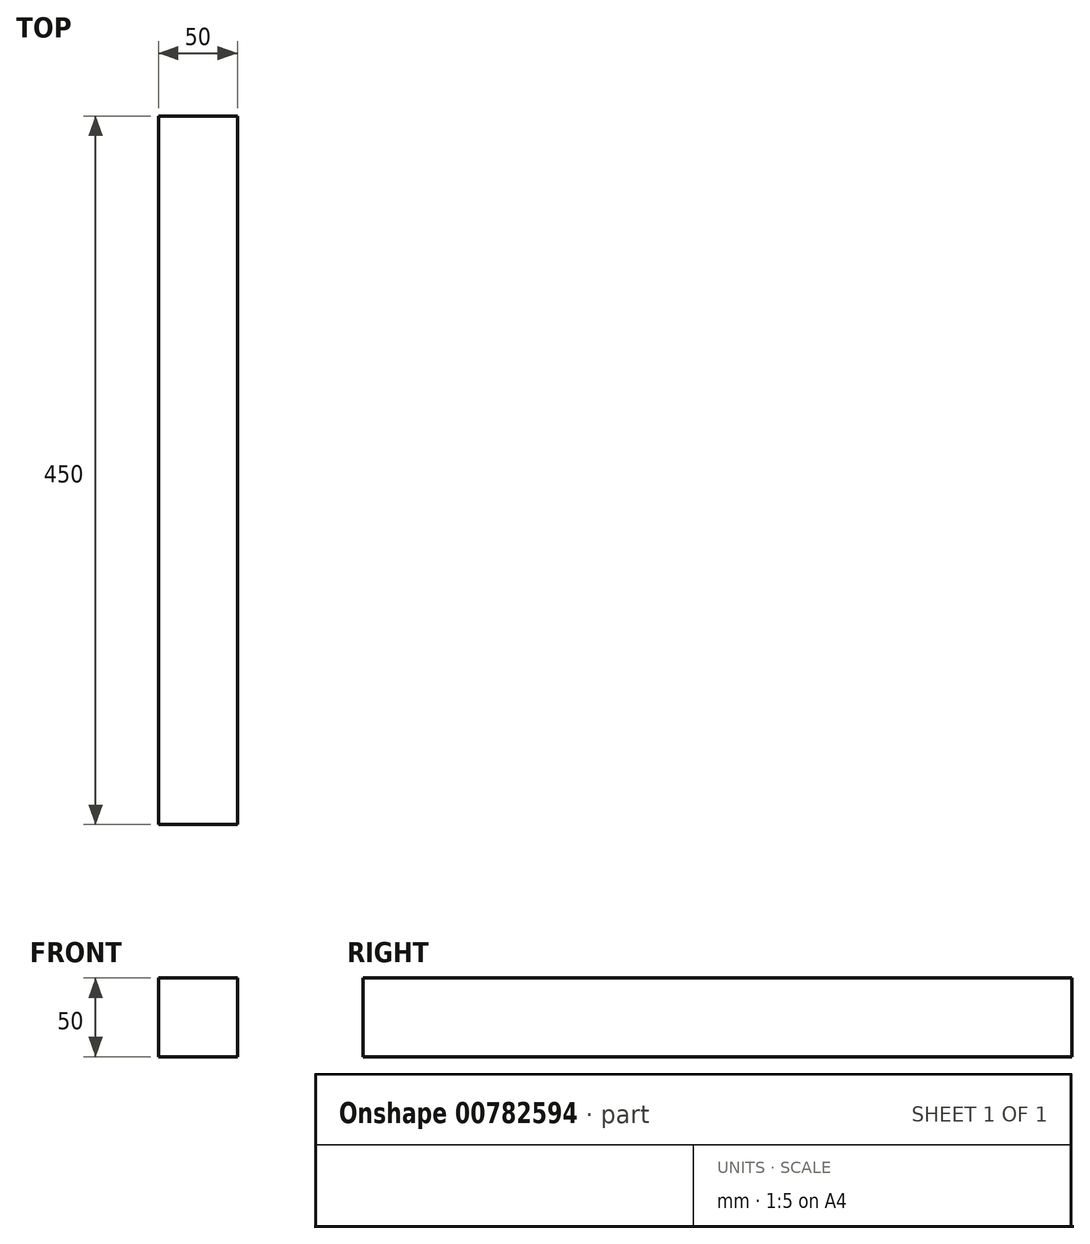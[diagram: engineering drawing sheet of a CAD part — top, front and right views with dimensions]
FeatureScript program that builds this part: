
annotation { "Feature Type Name" : "Feature", "Feature Type Description" : "" }
export const myFeature = defineFeature(function(context is Context, id is Id, definition is map)
    precondition{}
    {
        {
            var Q0;
            Q0=qCreatedBy(makeId("Front.planeOp"),FACE);
            var sketch = newSketch(context, id + "F0", { "sketchPlane" : qUnion([Q0])});
            skLineSegment(sketch, "E0.bottom", {"start": v(0, 0) * mm, "end": v(50, 0) * mm});
            skLineSegment(sketch, "E0.top", {"start": v(0, 50) * mm, "end": v(50, 50) * mm});
            skLineSegment(sketch, "E0.left", {"start": v(0, 0) * mm, "end": v(0, 50) * mm});
            skLineSegment(sketch, "E0.right", {"start": v(50, 0) * mm, "end": v(50, 50) * mm});
            skSolve(sketch);
        }
        {
            var Q0;
            Q0=qSketchRegion(id+"F0",true);
            extrude(context, id + "F1", {"entities" : qUnion([Q0]), "depth" : 450 * mm, "offsetDistance" : 25 * mm});
        }
    });
